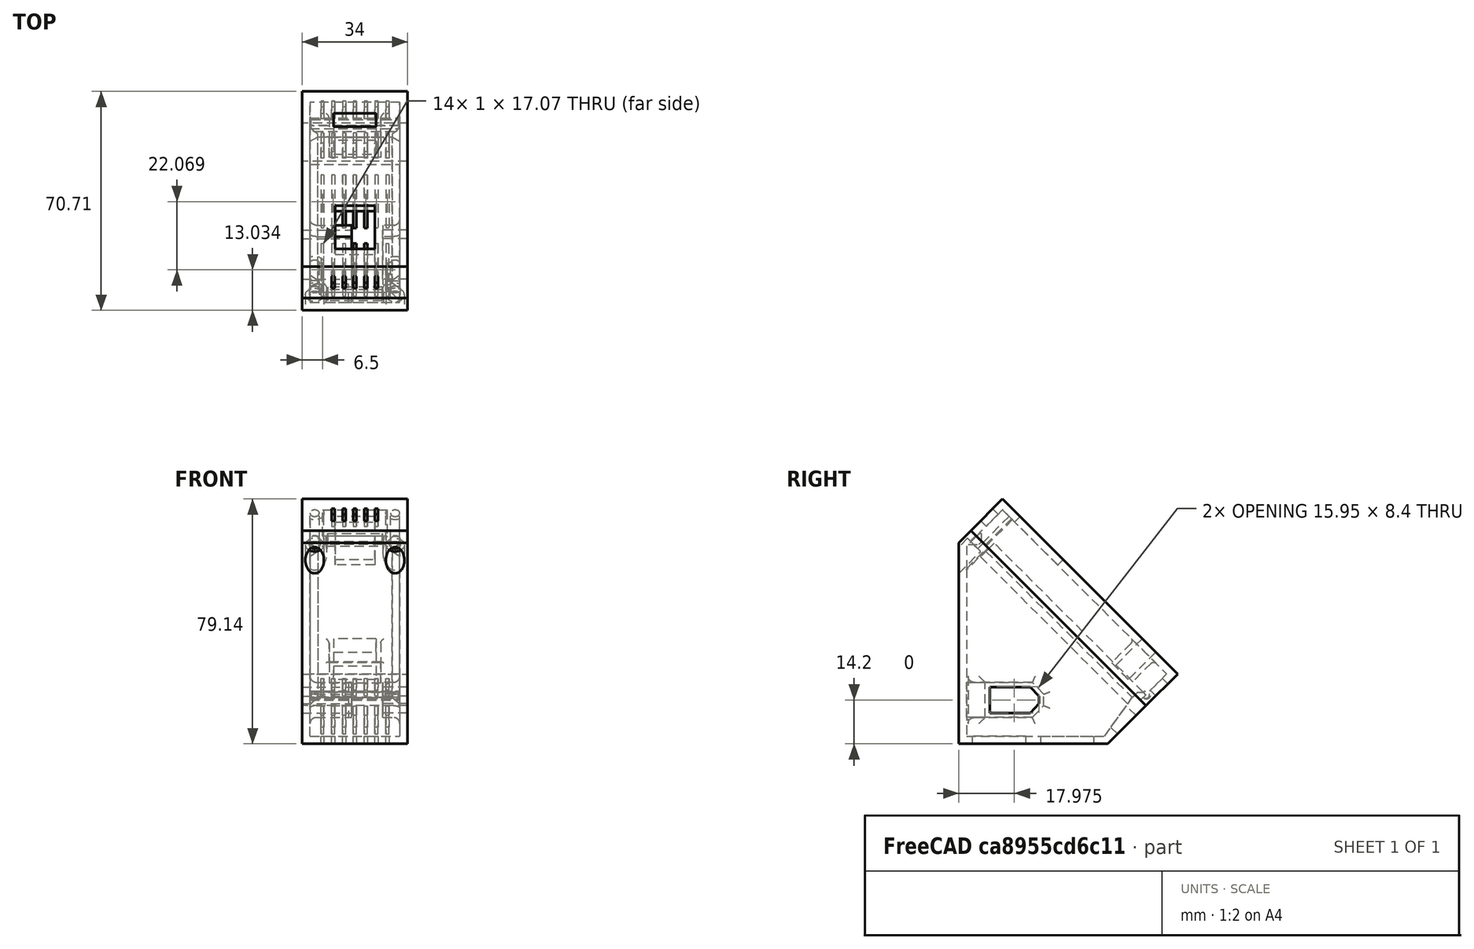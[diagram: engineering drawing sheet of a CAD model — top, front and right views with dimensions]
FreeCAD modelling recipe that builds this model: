
FCSTD DOCUMENT  (FreeCAD 0.18R4 (GitTag))
Label: usbSingleFavSep
License: All rights reserved
LicenseURL: http://en.wikipedia.org/wiki/All_rights_reserved
objects: Part::Feature×2, App::Part×2, Sketcher::SketchObject×2, PartDesign::Plane×1, PartDesign::ShapeBinder×1, PartDesign::Body×1
note: 7 computed .brp shape members not serialized (recipe doc carries the construction recipe); baked Part::Feature solids carry a one-line shape summary decoded from their .brp

FEATURE [Part::Feature] Part__Feature  label="USB PSU"
  shape: bbox 34 x 66.82 x 66.82 mm, 84 faces (baked)
FEATURE [App::Part] usb1_v1  label="usb1 v1"
  Group = -> [Part__Feature]
  Origin = -> Origin
  Placement = pos=(0,0,0) rot=(1,0,0;1.5708rad)
FEATURE [Part::Feature] Part__Feature001  label="USB PSU001"
  shape: bbox 34 x 65.85 x 68.89 mm, 167 faces (baked)
FEATURE [App::Part] usb1_v2  label="usb1 v2"
  Group = -> [Part__Feature001]
  Origin = -> Origin001
FEATURE [PartDesign::Plane] DatumPlane
  AttachmentOffset = pos=(0,0,-3) rot=(0,0,1;0rad)
  Length = 35.7232
  MapMode = 5
  Placement = pos=(0,0,-3) rot=(0,0,1;0rad)
  ResizeMode = 0
  Support = -> [XY_Plane002]
  Width = 79.1808
FEATURE [Sketcher::SketchObject] Sketch
  MapMode = 5
  Placement = pos=(0,0,-3) rot=(0,0,1;0rad)
  Support = -> [DatumPlane]
FEATURE [PartDesign::ShapeBinder] CopyPart__Feature001
  TraceSupport = false
FEATURE [Sketcher::SketchObject] Sketch001
  ExternalGeometry = -> [CopyPart__Feature001]
  MapMode = 5
  Placement = pos=(17,0,0) rot=(0.57735,0.57735,0.57735;2.0944rad)
  Support = -> [CopyPart__Feature001]
  constraints (1):
    c: Distance(g-3) = 5.5
FEATURE [PartDesign::Body] Body
  Group = -> [DatumPlane,Sketch,CopyPart__Feature001,Sketch001]
  Origin = -> Origin002
  Placement = pos=(0,0,0) rot=(1,0,0;1.5708rad)
